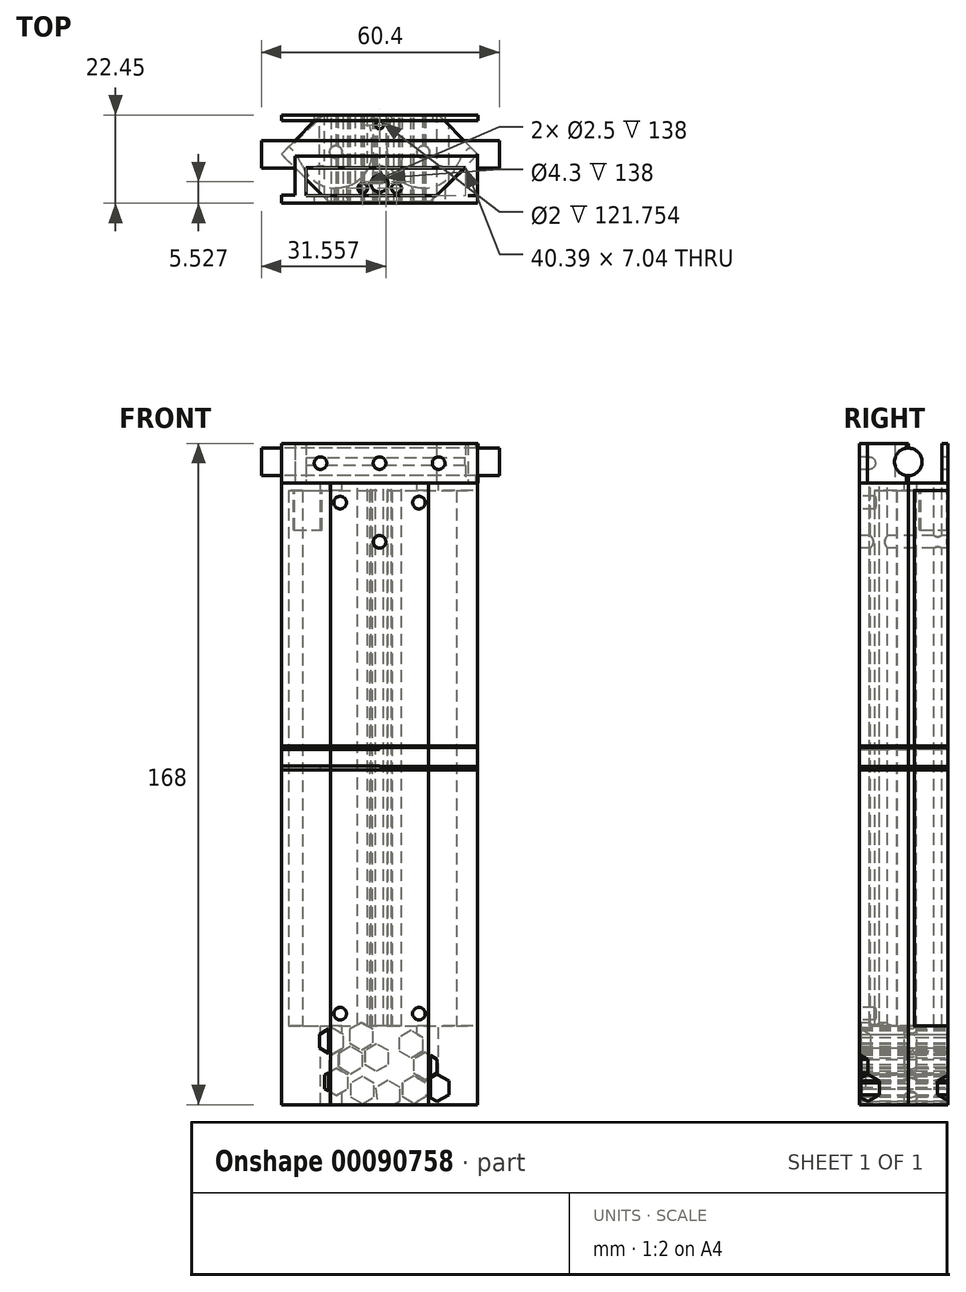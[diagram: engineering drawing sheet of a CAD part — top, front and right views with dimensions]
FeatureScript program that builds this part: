
annotation { "Feature Type Name" : "Feature", "Feature Type Description" : "" }
export const myFeature = defineFeature(function(context is Context, id is Id, definition is map)
    precondition{}
    {
        {
            var Q0;
            Q0=qCreatedBy(makeId("Top.planeOp"),FACE);
            var sketch = newSketch(context, id + "F0", { "sketchPlane" : qUnion([Q0])});
            skCircle(sketch, "E0.0", {"center": v(28.34, -87.3) * mm, "radius": 1 * mm});
            skCircle(sketch, "E0.1", {"center": v(39.24, -83.4) * mm, "radius": 2 * mm});
            skCircle(sketch, "E0.2", {"center": v(60.56, -76.3) * mm, "radius": 2.01 * mm});
            skCircle(sketch, "E0.3", {"center": v(29.67, -76.3) * mm, "radius": 9.48 * mm});
            skCircle(sketch, "E0.4", {"center": v(48.77, -76.3) * mm, "radius": 9.48 * mm});
            skLineSegment(sketch, "E0.5", {"start": v(64.18, -76.3) * mm, "end": v(14.3, -76.3) * mm});
            skLineSegment(sketch, "E0.6", {"start": v(14.3, -76.3) * mm, "end": v(24.27, -66.32) * mm});
            skLineSegment(sketch, "E0.7", {"start": v(24.27, -66.32) * mm, "end": v(52.19, -66.32) * mm});
            skLineSegment(sketch, "E0.8", {"start": v(52.19, -66.32) * mm, "end": v(64.18, -76.3) * mm});
            skCircle(sketch, "E0.9", {"center": v(50.63, -87.21) * mm, "radius": 1 * mm});
            skCircle(sketch, "E0.10", {"center": v(32.98, -87.04) * mm, "radius": 1 * mm});
            skCircle(sketch, "E0.11", {"center": v(45.91, -87.12) * mm, "radius": 1 * mm});
            skCircle(sketch, "E0.12", {"center": v(39.24, -69) * mm, "radius": 2 * mm});
            skLineSegment(sketch, "E0.13", {"start": v(26.76, -88.77) * mm, "end": v(51.7, -88.77) * mm});
            skCircle(sketch, "E0.14", {"center": v(17.86, -76.3) * mm, "radius": 2.02 * mm});
            skCircle(sketch, "E0.15", {"center": v(39.24, -69) * mm, "radius": 2 * mm});
            skCircle(sketch, "E0.16", {"center": v(39.24, -83.4) * mm, "radius": 2 * mm});
            skCircle(sketch, "E0.17", {"center": v(60.56, -76.3) * mm, "radius": 2.01 * mm});
            skCircle(sketch, "E0.18", {"center": v(17.86, -76.3) * mm, "radius": 2.02 * mm});
            skCircle(sketch, "E0.19", {"center": v(50.63, -87.21) * mm, "radius": 1 * mm});
            skCircle(sketch, "E0.20", {"center": v(28.34, -87.3) * mm, "radius": 1 * mm});
            skCircle(sketch, "E0.21", {"center": v(32.98, -87.04) * mm, "radius": 1 * mm});
            skCircle(sketch, "E0.22", {"center": v(45.91, -87.12) * mm, "radius": 1 * mm});
            skCircle(sketch, "E0.23", {"center": v(39.24, -69) * mm, "radius": 2 * mm});
            skCircle(sketch, "E0.24", {"center": v(39.24, -83.4) * mm, "radius": 2 * mm});
            skCircle(sketch, "E0.25", {"center": v(60.56, -76.3) * mm, "radius": 2.01 * mm});
            skCircle(sketch, "E0.26", {"center": v(17.86, -76.3) * mm, "radius": 2.02 * mm});
            skCircle(sketch, "E0.27", {"center": v(50.63, -87.21) * mm, "radius": 1 * mm});
            skCircle(sketch, "E0.28", {"center": v(28.34, -87.3) * mm, "radius": 1 * mm});
            skCircle(sketch, "E0.29", {"center": v(32.98, -87.04) * mm, "radius": 1 * mm});
            skCircle(sketch, "E0.30", {"center": v(45.91, -87.12) * mm, "radius": 1 * mm});
            skLineSegment(sketch, "E1", {"start": v(64.18, -76.3) * mm, "end": v(51.7, -88.77) * mm});
            skLineSegment(sketch, "E2", {"start": v(26.76, -88.77) * mm, "end": v(14.3, -76.3) * mm});
            skLineSegment(sketch, "E3", {"start": v(51.7, -88.77) * mm, "end": v(39.26, -101.25) * mm});
            skLineSegment(sketch, "E4", {"start": v(39.26, -101.25) * mm, "end": v(26.76, -88.77) * mm});
            skCircle(sketch, "E5.3", {"center": v(-36.32, -74.95) * mm, "radius": 9.2 * mm});
            skLineSegment(sketch, "E5.6", {"start": v(-50.16, -75.51) * mm, "end": v(-40.22, -65.55) * mm});
            skLineSegment(sketch, "E5.7", {"start": v(-40.22, -65.55) * mm, "end": v(-25.22, -65.56) * mm});
            skLineSegment(sketch, "E6", {"start": v(-12.73, -88) * mm, "end": v(-25.24, -100.46) * mm});
            skLineSegment(sketch, "E7", {"start": v(-25.24, -100.46) * mm, "end": v(-25.22, -65.56) * mm, "construction": true});
            skLineSegment(sketch, "E8", {"start": v(-50.16, -75.51) * mm, "end": v(-37.7, -87.98) * mm});
            skCircle(sketch, "E9.MirrorC", {"center": v(-14.12, -74.97) * mm, "radius": 9.2 * mm});
            skLineSegment(sketch, "E10.MirrorCS", {"start": v(-0.28, -75.54) * mm, "end": v(-25.24, -100.46) * mm});
            skLineSegment(sketch, "E11.MirrorCS", {"start": v(-0.28, -75.54) * mm, "end": v(-10.22, -65.57) * mm});
            skLineSegment(sketch, "E12.MirrorCS", {"start": v(-10.22, -65.57) * mm, "end": v(-25.22, -65.56) * mm});
            skLineSegment(sketch, "E13.MirrorCS", {"start": v(-37.73, -87.98) * mm, "end": v(-25.24, -100.46) * mm});
            skPoint(sketch, "E14.trimOffspring.start.orphan", {"position": v(-25.27, -75.46) * mm});
            skPoint(sketch, "E15.orphan", {"position": v(-50.27, -75.46) * mm});
            skLineSegment(sketch, "E16", {"start": v(-37.73, -87.98) * mm, "end": v(-12.73, -88) * mm});
            skFitSpline(sketch, "E17", {"points": [v(-27.12, -74.95) * mm, v(-29.63, -65.56) * mm, v(-72.25, -74.23) * mm], "startDerivative": vector(-1.55, 35.66) * mm, "endDerivative": vector(-79.61, -26.9) * mm});
            skFitSpline(sketch, "E18.MirrorCS", {"points": [v(-23.32, -74.96) * mm, v(-20.8, -65.56) * mm, v(21.8, -74.28) * mm], "startDerivative": vector(1.59, 35.66) * mm, "endDerivative": vector(79.58, -26.99) * mm});
            skFitSpline(sketch, "E19", {"points": [v(-44.25, -79.62) * mm, v(-48.33, -73.68) * mm, v(-51.27, -73.94) * mm], "startDerivative": vector(-6.44, 12.9) * mm, "endDerivative": vector(-7.7, -2.7) * mm});
            skFitSpline(sketch, "E20.MirrorCS", {"points": [v(-6.2, -79.64) * mm, v(-2.1, -73.7) * mm, v(0.83, -73.97) * mm], "startDerivative": vector(6.46, 12.9) * mm, "endDerivative": vector(7.7, -2.71) * mm});
            skSolve(sketch);
        }
        {
            var Q0;
            {var subQ18=sQuery(id+"F0.wireOp",EDGE,"E8");Q0=makeQuery(id+"F0.imprint","IMPRINT",FACE,{"disambiguationData":[TD([[makeQuery(id+"F0.imprint","IMPRINT",EDGE,{"derivedFrom":subQ18}),1.0]])]});}
            extrude(context, id + "F1", {"entities" : qUnion([Q0]), "depth" : 138 * mm});
        }
        {
            var Q0;
            Q0=makeQuery(id+"F1.opExtrude","CAP_FACE",FACE,{"disambiguationData":[OSD([sQuery(id+"F0.wireOp",EDGE,"E5.3"),sQuery(id+"F0.wireOp",EDGE,"E5.6"),sQuery(id+"F0.wireOp",EDGE,"E5.7"),sQuery(id+"F0.wireOp",EDGE,"E8"),sQuery(id+"F0.wireOp",EDGE,"E9.MirrorC"),sQuery(id+"F0.wireOp",EDGE,"E10.MirrorCS"),sQuery(id+"F0.wireOp",EDGE,"E11.MirrorCS"),sQuery(id+"F0.wireOp",EDGE,"E12.MirrorCS"),sQuery(id+"F0.wireOp",EDGE,"E16"),sQuery(id+"F0.wireOp",EDGE,"E17"),sQuery(id+"F0.wireOp",EDGE,"28ce3c09-6c9a-4552-adf3-a01f3755cea0"),sQuery(id+"F0.wireOp",EDGE,"77121457-b61a-4b0d-bc9d-ba2fe8860e380.MirrorCS"),sQuery(id+"F0.wireOp",EDGE,"E18.MirrorCS")])],"isStart":false});
            var sketch = newSketch(context, id + "F2", { "sketchPlane" : qUnion([Q0])});
            skLineSegment(sketch, "E21.0", {"start": v(-40.22, -65.55) * mm, "end": v(-25.22, -65.56) * mm});
            skLineSegment(sketch, "E21.1", {"start": v(-10.22, -65.57) * mm, "end": v(-25.22, -65.56) * mm});
            skLineSegment(sketch, "E21.2", {"start": v(-0.28, -75.54) * mm, "end": v(-10.22, -65.57) * mm});
            skLineSegment(sketch, "E21.3", {"start": v(-0.28, -75.54) * mm, "end": v(-12.75, -88) * mm});
            skLineSegment(sketch, "E21.4", {"start": v(-50.16, -75.51) * mm, "end": v(-37.7, -87.98) * mm});
            skLineSegment(sketch, "E21.5", {"start": v(-50.16, -75.51) * mm, "end": v(-40.22, -65.55) * mm});
            skLineSegment(sketch, "E22.0", {"start": v(-37.7, -87.98) * mm, "end": v(-12.75, -88) * mm});
            skPoint(sketch, "E23.orphan", {"position": v(-37.7, -87.98) * mm});
            skPoint(sketch, "E24.orphan", {"position": v(-25.24, -100.46) * mm});
            skSolve(sketch);
        }
        {
            var Q0;
            Q0 = qSketchRegion(id + "F2", true);
            var Q1;
            Q1=sQuery(id+"F0.wireOp",EDGE,"E12.MirrorCS");
            var Q2;
            Q2=sQuery(id+"F0.wireOp",EDGE,"E5.7");
            var Q3;
            Q3=sQuery(id+"F0.wireOp",EDGE,"E5.6");
            var Q4;
            Q4=sQuery(id+"F0.wireOp",EDGE,"E8");
            var Q5;
            Q5=sQuery(id+"F0.wireOp",EDGE,"E6");
            var Q6;
            Q6=sQuery(id+"F0.wireOp",EDGE,"E10.MirrorCS");
            var Q7;
            Q7=sQuery(id+"F0.wireOp",EDGE,"E11.MirrorCS");
            extrude(context, id + "F3", {"entities" : qUnion([Q0]), "operationType" : NewBodyOperationType.ADD, "surfaceEntities" : qUnion([Q1, Q2, Q3, Q4, Q5, Q6, Q7]), "oppositeDirection" : true, "depth" : 2 * mm});
        }
        {
            var Q0;
            Q0=makeQuery(id+"F1.opExtrude","SWEPT_FACE",FACE,{"disambiguationData":[OSD([sQuery(id+"F0.wireOp",EDGE,"E16")])]});
            var sketch = newSketch(context, id + "F4", { "sketchPlane" : qUnion([Q0])});
            skLineSegment(sketch, "E25", {"start": v(-25.18, 140) * mm, "end": v(-25.18, 71.2) * mm, "construction": true});
            skLineSegment(sketch, "E26.0", {"start": v(-50.12, 138) * mm, "end": v(-50.12, 0) * mm, "construction": true});
            skLineSegment(sketch, "E27", {"start": v(-50.12, 65.9) * mm, "end": v(-50.12, 65.1) * mm});
            skLineSegment(sketch, "E28", {"start": v(-50.12, 65.1) * mm, "end": v(-0.24, 65.1) * mm});
            skLineSegment(sketch, "E29", {"start": v(-0.24, 65.1) * mm, "end": v(-0.24, 65.9) * mm});
            skLineSegment(sketch, "E30", {"start": v(-50.12, 70.8) * mm, "end": v(-50.12, 71.2) * mm});
            skLineSegment(sketch, "E31", {"start": v(-50.12, 71.2) * mm, "end": v(-0.24, 71.2) * mm});
            skLineSegment(sketch, "E32.MirrorCS", {"start": v(-50.12, 70.4) * mm, "end": v(-0.24, 70.8) * mm});
            skLineSegment(sketch, "E33", {"start": v(-0.24, 71.2) * mm, "end": v(-0.24, 70.8) * mm});
            skLineSegment(sketch, "E34", {"start": v(-50.12, 70.8) * mm, "end": v(-50.12, 70.4) * mm});
            skLineSegment(sketch, "E35.0", {"start": v(-20.76, 136) * mm, "end": v(-10.18, 136) * mm, "construction": true});
            skLineSegment(sketch, "E36", {"start": v(-0.24, 65.9) * mm, "end": v(-50.12, 65.9) * mm});
            skPoint(sketch, "E37.orphan", {"position": v(-50.12, 69) * mm});
            skLineSegment(sketch, "E38", {"start": v(-25.18, 65.1) * mm, "end": v(-25.18, 65.9) * mm});
            skLineSegment(sketch, "E39.trimOffspring", {"start": v(-25.18, 65.1) * mm, "end": v(-25.18, 0) * mm, "construction": true});
            skLineSegment(sketch, "E40.trimOffspring", {"start": v(-25.18, 70.6) * mm, "end": v(-25.18, 65.9) * mm, "construction": true});
            skLineSegment(sketch, "E41", {"start": v(-25.18, 70.6) * mm, "end": v(-25.18, 71.2) * mm});
            skLineSegment(sketch, "E42", {"start": v(-50.12, 65.9) * mm, "end": v(-50.12, 66.1) * mm});
            skLineSegment(sketch, "E43", {"start": v(-50.12, 66.1) * mm, "end": v(-25.18, 66.1) * mm});
            skLineSegment(sketch, "E44", {"start": v(-25.18, 66.1) * mm, "end": v(-25.18, 65.9) * mm});
            skLineSegment(sketch, "E45", {"start": v(-50.12, 65.5) * mm, "end": v(-25.18, 65.5) * mm, "construction": true});
            skLineSegment(sketch, "E46", {"start": v(-50.12, 70.4) * mm, "end": v(-50.12, 70.2) * mm});
            skLineSegment(sketch, "E47", {"start": v(-50.12, 70.2) * mm, "end": v(-25.18, 70.2) * mm});
            skLineSegment(sketch, "E48", {"start": v(-25.18, 70.2) * mm, "end": v(-25.18, 70.6) * mm});
            skSolve(sketch);
        }
        {
            var Q0;
            Q0 = qSketchRegion(id + "F4", true);
            var Q1;
            Q1=makeQuery(id+"F3.boolean.opBoolean","MERGE",FACE,{"derivedFrom":[makeQuery(id+"F1.opExtrude","SWEPT_FACE",FACE,{"disambiguationData":[OSD([sQuery(id+"F0.wireOp",EDGE,"E5.7"),sQuery(id+"F0.wireOp",EDGE,"E12.MirrorCS")])]}),makeQuery(id+"F3.opExtrude","SWEPT_FACE",FACE,{"disambiguationData":[OSD([sQuery(id+"F2.wireOp",EDGE,"E21.0"),sQuery(id+"F2.wireOp",EDGE,"E21.1")])]})]});
            extrude(context, id + "F5", {"entities" : qUnion([Q0]), "endBound" : BoundingType.UP_TO_SURFACE, "oppositeDirection" : true, "endBoundEntityFace" : qUnion([Q1]), "depth" : 25 * mm});
        }
        {
            var Q0;
            {var subQ18=sQuery(id+"F0.wireOp",EDGE,"E8");Q0=makeQuery(id+"F0.imprint","IMPRINT",FACE,{"disambiguationData":[TD([[makeQuery(id+"F0.imprint","IMPRINT",EDGE,{"derivedFrom":subQ18}),1.0]])]});}
            var sketch = newSketch(context, id + "F6", { "sketchPlane" : qUnion([Q0])});
            skLineSegment(sketch, "E49.0", {"start": v(-50.16, -75.51) * mm, "end": v(-40.22, -65.55) * mm});
            skLineSegment(sketch, "E49.1", {"start": v(-40.22, -65.55) * mm, "end": v(-25.22, -65.56) * mm});
            skLineSegment(sketch, "E49.2", {"start": v(-10.22, -65.57) * mm, "end": v(-25.22, -65.56) * mm});
            skLineSegment(sketch, "E49.3", {"start": v(-0.28, -75.54) * mm, "end": v(-10.22, -65.57) * mm});
            skLineSegment(sketch, "E49.4", {"start": v(-0.28, -75.54) * mm, "end": v(-12.75, -88) * mm});
            skLineSegment(sketch, "E49.5", {"start": v(-37.73, -87.98) * mm, "end": v(-12.73, -88) * mm});
            skLineSegment(sketch, "E49.6", {"start": v(-50.16, -75.51) * mm, "end": v(-37.7, -87.98) * mm});
            skPoint(sketch, "E50.orphan", {"position": v(-25.24, -100.46) * mm});
            skPoint(sketch, "E51.orphan", {"position": v(-37.7, -87.98) * mm});
            skLineSegment(sketch, "E52.2", {"start": v(-0.3, -88) * mm, "end": v(-50.17, -87.97) * mm});
            skSolve(sketch);
        }
        {
            var Q0;
            Q0 = qSketchRegion(id + "F6", true);
            var Q1;
            Q1 = qSketchRegion(id + "F8", true);
            extrude(context, id + "F7", {"entities" : qUnion([Q0, Q1]), "operationType" : NewBodyOperationType.ADD, "oppositeDirection" : true, "depth" : 20 * mm});
        }
        {
            var Q0;
            Q0=makeQuery(id+"F7.boolean.opBoolean","MERGE",FACE,{"derivedFrom":[makeQuery(id+"F3.boolean.opBoolean","MERGE",FACE,{"derivedFrom":[makeQuery(id+"F1.opExtrude","SWEPT_FACE",FACE,{"disambiguationData":[OSD([sQuery(id+"F0.wireOp",EDGE,"E5.7"),sQuery(id+"F0.wireOp",EDGE,"E12.MirrorCS")])]}),makeQuery(id+"F3.opExtrude","SWEPT_FACE",FACE,{"disambiguationData":[OSD([sQuery(id+"F2.wireOp",EDGE,"E21.0"),sQuery(id+"F2.wireOp",EDGE,"E21.1")])]})]}),makeQuery(id+"F7.opExtrude","SWEPT_FACE",FACE,{"disambiguationData":[OSD([sQuery(id+"F6.wireOp",EDGE,"E49.1"),sQuery(id+"F6.wireOp",EDGE,"E49.2")])]})]});
            var sketch = newSketch(context, id + "F8", { "sketchPlane" : qUnion([Q0])});
            skCircle(sketch, "E53.cCircle", {"center": v(36.14, -14.2) * mm, "radius": 3 * mm, "construction": true});
            skLineSegment(sketch, "E53.0", {"start": v(33.14, -12.47) * mm, "end": v(36.14, -10.74) * mm});
            skLineSegment(sketch, "E53.1", {"start": v(36.14, -10.74) * mm, "end": v(39.14, -12.47) * mm});
            skLineSegment(sketch, "E53.2", {"start": v(39.14, -12.47) * mm, "end": v(39.14, -15.94) * mm});
            skLineSegment(sketch, "E53.3", {"start": v(39.14, -15.94) * mm, "end": v(36.14, -17.67) * mm});
            skLineSegment(sketch, "E53.4", {"start": v(36.14, -17.67) * mm, "end": v(33.14, -15.94) * mm});
            skLineSegment(sketch, "E53.5", {"start": v(33.14, -15.94) * mm, "end": v(33.14, -12.47) * mm});
            skPoint(sketch, "E53.0.midPoint", {"position": v(34.64, -11.6) * mm});
            skLineSegment(sketch, "E54", {"start": v(36.14, -17.67) * mm, "end": v(36.14, 0) * mm, "construction": true});
            skCircle(sketch, "E55.cCircle", {"center": v(37.4, -3.84) * mm, "radius": 3 * mm, "construction": true});
            skLineSegment(sketch, "E55.0", {"start": v(34.4, -2.1) * mm, "end": v(37.4, -0.38) * mm});
            skLineSegment(sketch, "E55.1", {"start": v(37.4, -0.38) * mm, "end": v(40.4, -2.1) * mm});
            skLineSegment(sketch, "E55.2", {"start": v(40.4, -2.1) * mm, "end": v(40.4, -5.57) * mm});
            skLineSegment(sketch, "E55.3", {"start": v(40.4, -5.57) * mm, "end": v(37.4, -7.3) * mm});
            skLineSegment(sketch, "E55.4", {"start": v(37.4, -7.3) * mm, "end": v(34.4, -5.57) * mm});
            skLineSegment(sketch, "E55.5", {"start": v(34.4, -5.57) * mm, "end": v(34.4, -2.1) * mm});
            skPoint(sketch, "E55.0.midPoint", {"position": v(35.9, -1.24) * mm});
            skCircle(sketch, "E56.cCircle", {"center": v(32.54, -8.66) * mm, "radius": 3 * mm, "construction": true});
            skLineSegment(sketch, "E56.0", {"start": v(29.54, -6.93) * mm, "end": v(32.54, -5.2) * mm});
            skLineSegment(sketch, "E56.1", {"start": v(32.54, -5.2) * mm, "end": v(35.54, -6.93) * mm});
            skLineSegment(sketch, "E56.2", {"start": v(35.54, -6.93) * mm, "end": v(35.54, -10.4) * mm});
            skLineSegment(sketch, "E56.3", {"start": v(35.54, -10.4) * mm, "end": v(32.54, -12.13) * mm});
            skLineSegment(sketch, "E56.4", {"start": v(32.54, -12.13) * mm, "end": v(29.54, -10.4) * mm});
            skLineSegment(sketch, "E56.5", {"start": v(29.54, -10.4) * mm, "end": v(29.54, -6.93) * mm});
            skPoint(sketch, "E56.0.midPoint", {"position": v(31.04, -6.07) * mm});
            skCircle(sketch, "E57.cCircle", {"center": v(29.54, -16.34) * mm, "radius": 3 * mm, "construction": true});
            skLineSegment(sketch, "E57.0", {"start": v(26.54, -14.6) * mm, "end": v(29.54, -12.87) * mm});
            skLineSegment(sketch, "E57.1", {"start": v(29.54, -12.87) * mm, "end": v(32.54, -14.6) * mm});
            skLineSegment(sketch, "E57.2", {"start": v(32.54, -14.6) * mm, "end": v(32.54, -18.07) * mm});
            skLineSegment(sketch, "E57.3", {"start": v(32.54, -18.07) * mm, "end": v(29.54, -19.8) * mm});
            skLineSegment(sketch, "E57.4", {"start": v(29.54, -19.8) * mm, "end": v(26.54, -18.07) * mm});
            skLineSegment(sketch, "E57.5", {"start": v(26.54, -18.07) * mm, "end": v(26.54, -14.6) * mm});
            skPoint(sketch, "E57.0.midPoint", {"position": v(28.04, -13.74) * mm});
            skCircle(sketch, "E58.cCircle", {"center": v(23.01, -17.31) * mm, "radius": 3 * mm, "construction": true});
            skLineSegment(sketch, "E58.0", {"start": v(20.01, -15.58) * mm, "end": v(23.01, -13.85) * mm});
            skLineSegment(sketch, "E58.1", {"start": v(23.01, -13.85) * mm, "end": v(26.26, -15.72) * mm});
            skLineSegment(sketch, "E58.2", {"start": v(26.26, -15.72) * mm, "end": v(25.7, -19.8) * mm});
            skLineSegment(sketch, "E58.4", {"start": v(21.51, -19.9) * mm, "end": v(20.01, -19.04) * mm});
            skLineSegment(sketch, "E58.5", {"start": v(20.01, -19.04) * mm, "end": v(20.01, -15.58) * mm});
            skPoint(sketch, "E58.0.midPoint", {"position": v(21.51, -14.71) * mm});
            skCircle(sketch, "E59.cCircle", {"center": v(29.82, -2.61) * mm, "radius": 3 * mm, "construction": true});
            skLineSegment(sketch, "E59.0", {"start": v(26.82, -0.88) * mm, "end": v(29.82, 0.85) * mm});
            skLineSegment(sketch, "E59.1", {"start": v(29.82, 0.85) * mm, "end": v(32.82, -0.88) * mm});
            skLineSegment(sketch, "E59.2", {"start": v(32.82, -0.88) * mm, "end": v(32.82, -4.35) * mm});
            skLineSegment(sketch, "E59.3", {"start": v(32.82, -4.35) * mm, "end": v(29.82, -6.08) * mm});
            skLineSegment(sketch, "E59.4", {"start": v(29.82, -6.08) * mm, "end": v(26.82, -4.35) * mm});
            skLineSegment(sketch, "E59.5", {"start": v(26.82, -4.35) * mm, "end": v(26.82, -0.88) * mm});
            skPoint(sketch, "E59.0.midPoint", {"position": v(28.32, -0.02) * mm});
            skCircle(sketch, "E60.cCircle", {"center": v(25.94, -8) * mm, "radius": 3 * mm, "construction": true});
            skLineSegment(sketch, "E60.0", {"start": v(22.94, -6.27) * mm, "end": v(25.94, -4.53) * mm});
            skLineSegment(sketch, "E60.1", {"start": v(25.94, -4.53) * mm, "end": v(28.94, -6.27) * mm});
            skLineSegment(sketch, "E60.2", {"start": v(28.94, -6.27) * mm, "end": v(28.94, -9.73) * mm});
            skLineSegment(sketch, "E60.3", {"start": v(28.94, -9.73) * mm, "end": v(25.94, -11.46) * mm});
            skLineSegment(sketch, "E60.4", {"start": v(25.94, -11.46) * mm, "end": v(22.94, -9.73) * mm});
            skLineSegment(sketch, "E60.5", {"start": v(22.94, -9.73) * mm, "end": v(22.94, -6.27) * mm});
            skPoint(sketch, "E60.0.midPoint", {"position": v(24.44, -5.4) * mm});
            skCircle(sketch, "E61.cCircle", {"center": v(16.41, -16.2) * mm, "radius": 3 * mm, "construction": true});
            skLineSegment(sketch, "E61.0", {"start": v(13.41, -14.46) * mm, "end": v(16.41, -12.73) * mm});
            skLineSegment(sketch, "E61.1", {"start": v(16.41, -12.73) * mm, "end": v(19.41, -14.46) * mm});
            skLineSegment(sketch, "E61.2", {"start": v(19.41, -14.46) * mm, "end": v(19.41, -17.93) * mm});
            skLineSegment(sketch, "E61.3", {"start": v(19.41, -17.93) * mm, "end": v(16.41, -19.66) * mm});
            skLineSegment(sketch, "E61.4", {"start": v(16.41, -19.66) * mm, "end": v(13.41, -17.93) * mm});
            skLineSegment(sketch, "E61.5", {"start": v(13.41, -17.93) * mm, "end": v(13.41, -14.46) * mm});
            skPoint(sketch, "E61.0.midPoint", {"position": v(14.91, -13.6) * mm});
            skLineSegment(sketch, "E62", {"start": v(25.7, -19.8) * mm, "end": v(21.51, -19.9) * mm});
            skLineSegment(sketch, "E63.5", {"start": v(14.2, -17.46) * mm, "end": v(14.2, -14) * mm});
            skPoint(sketch, "E63.0.midPoint", {"position": v(15.7, -13.13) * mm});
            skCircle(sketch, "E64.cCircle", {"center": v(17.2, -4.65) * mm, "radius": 3 * mm, "construction": true});
            skLineSegment(sketch, "E64.0", {"start": v(14.2, -2.91) * mm, "end": v(17.2, -1.18) * mm});
            skLineSegment(sketch, "E64.1", {"start": v(17.2, -1.18) * mm, "end": v(20.2, -2.91) * mm});
            skLineSegment(sketch, "E64.2", {"start": v(20.2, -2.91) * mm, "end": v(20.2, -6.38) * mm});
            skLineSegment(sketch, "E64.3", {"start": v(20.2, -6.38) * mm, "end": v(17.2, -8.1) * mm});
            skLineSegment(sketch, "E64.4", {"start": v(17.2, -8.1) * mm, "end": v(14.2, -6.38) * mm});
            skLineSegment(sketch, "E64.5", {"start": v(14.2, -6.38) * mm, "end": v(14.2, -2.91) * mm});
            skPoint(sketch, "E64.0.midPoint", {"position": v(15.7, -2.05) * mm});
            skCircle(sketch, "E65.cCircle", {"center": v(13.6, -10.19) * mm, "radius": 3 * mm, "construction": true});
            skLineSegment(sketch, "E65.0", {"start": v(10.6, -8.46) * mm, "end": v(13.6, -6.72) * mm});
            skLineSegment(sketch, "E65.1", {"start": v(13.6, -6.72) * mm, "end": v(16.6, -8.46) * mm});
            skLineSegment(sketch, "E65.2", {"start": v(16.6, -8.46) * mm, "end": v(16.6, -11.92) * mm});
            skLineSegment(sketch, "E65.3", {"start": v(16.6, -11.92) * mm, "end": v(13.6, -13.65) * mm});
            skLineSegment(sketch, "E65.4", {"start": v(13.6, -13.65) * mm, "end": v(10.6, -11.92) * mm});
            skLineSegment(sketch, "E65.5", {"start": v(10.6, -11.92) * mm, "end": v(10.6, -8.46) * mm});
            skPoint(sketch, "E65.0.midPoint", {"position": v(12.1, -7.59) * mm});
            skCircle(sketch, "E66.cCircle", {"center": v(10.6, -15.73) * mm, "radius": 3 * mm, "construction": true});
            skLineSegment(sketch, "E66.0", {"start": v(7.6, -14) * mm, "end": v(10.6, -12.27) * mm});
            skLineSegment(sketch, "E66.1", {"start": v(10.6, -12.27) * mm, "end": v(13.6, -14) * mm});
            skLineSegment(sketch, "E66.2", {"start": v(13.6, -14) * mm, "end": v(13.6, -17.46) * mm});
            skLineSegment(sketch, "E66.3", {"start": v(13.6, -17.46) * mm, "end": v(10.6, -19.2) * mm});
            skLineSegment(sketch, "E66.4", {"start": v(10.6, -19.2) * mm, "end": v(7.6, -17.46) * mm});
            skLineSegment(sketch, "E66.5", {"start": v(7.6, -17.46) * mm, "end": v(7.6, -14) * mm});
            skPoint(sketch, "E66.0.midPoint", {"position": v(9.1, -13.13) * mm});
            skSolve(sketch);
        }
        {
            var Q0;
            Q0 = qSketchRegion(id + "F8", true);
            var Q1;
            Q1=sQuery(id+"F8.wireOp",EDGE,"a0639ec5-36db-4593-97fa-c94961bb7019.1");
            var Q2;
            Q2=sQuery(id+"F8.wireOp",EDGE,"55600522-a46f-4de3-be34-bca631a758cf.4");
            var Q3;
            Q3=sQuery(id+"F8.wireOp",EDGE,"ffd1e3c1-856c-4fb0-91cf-635109e7a11e.5");
            var Q4;
            Q4=makeQuery(id+"F7.boolean.opBoolean","MERGE",FACE,{"derivedFrom":[makeQuery(id+"F1.opExtrude","SWEPT_FACE",FACE,{"disambiguationData":[OSD([sQuery(id+"F0.wireOp",EDGE,"E16")])]}),makeQuery(id+"F7.opExtrude","SWEPT_FACE",FACE,{"disambiguationData":[OSD([sQuery(id+"F6.wireOp",EDGE,"E52.2")])]})]});
            var Q5;
            Q5=makeQuery(id+"F1.opExtrude","SWEPT_BODY",BODY,{"disambiguationData":[OSD([sQuery(id+"F0.wireOp",EDGE,"E5.3"),sQuery(id+"F0.wireOp",EDGE,"E5.6"),sQuery(id+"F0.wireOp",EDGE,"E5.7"),sQuery(id+"F0.wireOp",EDGE,"E8"),sQuery(id+"F0.wireOp",EDGE,"E9.MirrorC"),sQuery(id+"F0.wireOp",EDGE,"E10.MirrorCS"),sQuery(id+"F0.wireOp",EDGE,"E11.MirrorCS"),sQuery(id+"F0.wireOp",EDGE,"E12.MirrorCS"),sQuery(id+"F0.wireOp",EDGE,"E16"),sQuery(id+"F0.wireOp",EDGE,"E17"),sQuery(id+"F0.wireOp",EDGE,"E18.MirrorCS"),sQuery(id+"F0.wireOp",EDGE,"E19"),sQuery(id+"F0.wireOp",EDGE,"E20.MirrorCS")])]});
            extrude(context, id + "F9", {"entities" : qUnion([Q0]), "operationType" : NewBodyOperationType.REMOVE, "surfaceEntities" : qUnion([Q1, Q2, Q3]), "oppositeDirection" : true, "endBoundEntityFace" : qUnion([Q4]), "endBoundEntityBody" : qUnion([Q5]), "depth" : 22 * mm});
        }
        {
            var Q0;
            Q0=makeQuery(id+"F3.boolean.opBoolean","MERGE",FACE,{"derivedFrom":[makeQuery(id+"F1.opExtrude","CAP_FACE",FACE,{"disambiguationData":[OSD([sQuery(id+"F0.wireOp",EDGE,"E5.3"),sQuery(id+"F0.wireOp",EDGE,"E5.6"),sQuery(id+"F0.wireOp",EDGE,"E5.7"),sQuery(id+"F0.wireOp",EDGE,"E8"),sQuery(id+"F0.wireOp",EDGE,"E9.MirrorC"),sQuery(id+"F0.wireOp",EDGE,"E10.MirrorCS"),sQuery(id+"F0.wireOp",EDGE,"E11.MirrorCS"),sQuery(id+"F0.wireOp",EDGE,"E12.MirrorCS"),sQuery(id+"F0.wireOp",EDGE,"E16"),sQuery(id+"F0.wireOp",EDGE,"E17"),sQuery(id+"F0.wireOp",EDGE,"28ce3c09-6c9a-4552-adf3-a01f3755cea0"),sQuery(id+"F0.wireOp",EDGE,"77121457-b61a-4b0d-bc9d-ba2fe8860e380.MirrorCS"),sQuery(id+"F0.wireOp",EDGE,"E18.MirrorCS")])],"isStart":false}),makeQuery(id+"F3.opExtrude","CAP_FACE",FACE,{"disambiguationData":[OSD([sQuery(id+"F2.wireOp",EDGE,"E21.0"),sQuery(id+"F2.wireOp",EDGE,"E21.1"),sQuery(id+"F2.wireOp",EDGE,"E21.2"),sQuery(id+"F2.wireOp",EDGE,"E21.3"),sQuery(id+"F2.wireOp",EDGE,"E21.4"),sQuery(id+"F2.wireOp",EDGE,"E21.5"),sQuery(id+"F2.wireOp",EDGE,"E22.0")])],"isStart":true})]});
            var sketch = newSketch(context, id + "F10", { "sketchPlane" : qUnion([Q0])});
            skLineSegment(sketch, "E67.0", {"start": v(-0.28, -65.57) * mm, "end": v(-50.15, -65.55) * mm});
            skLineSegment(sketch, "E67.1", {"start": v(-50.15, -65.55) * mm, "end": v(-50.17, -87.97) * mm});
            skLineSegment(sketch, "E67.2", {"start": v(-50.17, -87.97) * mm, "end": v(-0.3, -88) * mm});
            skLineSegment(sketch, "E67.3", {"start": v(-0.28, -65.57) * mm, "end": v(-0.3, -88) * mm});
            skLineSegment(sketch, "E67.4", {"start": v(-0.28, -75.54) * mm, "end": v(-10.22, -65.57) * mm});
            skLineSegment(sketch, "E67.5", {"start": v(-50.16, -75.51) * mm, "end": v(-40.22, -65.55) * mm});
            skLineSegment(sketch, "E67.6", {"start": v(-50.16, -75.51) * mm, "end": v(-37.7, -87.98) * mm});
            skLineSegment(sketch, "E67.7", {"start": v(-0.28, -75.54) * mm, "end": v(-12.75, -88) * mm});
            skPoint(sketch, "E68.orphan", {"position": v(-37.7, -87.98) * mm});
            skPoint(sketch, "E69.orphan", {"position": v(-25.24, -100.46) * mm});
            skSolve(sketch);
        }
        {
            var Q0;
            {var subQ0=sQuery(id+"F10.wireOp",EDGE,"E67.4");Q0=makeQuery(id+"F10.imprint","IMPRINT",FACE,{"disambiguationData":[TD([[makeQuery(id+"F10.imprint","IMPRINT",EDGE,{"derivedFrom":subQ0}),-1.0]])]});}
            var Q1;
            {var subQ0=sQuery(id+"F10.wireOp",EDGE,"E67.7");Q1=makeQuery(id+"F10.imprint","IMPRINT",FACE,{"disambiguationData":[TD([[makeQuery(id+"F10.imprint","IMPRINT",EDGE,{"derivedFrom":subQ0}),1.0]])]});}
            var Q2;
            {var subQ0=sQuery(id+"F10.wireOp",EDGE,"E67.6");Q2=makeQuery(id+"F10.imprint","IMPRINT",FACE,{"disambiguationData":[TD([[makeQuery(id+"F10.imprint","IMPRINT",EDGE,{"derivedFrom":subQ0}),-1.0]])]});}
            var Q3;
            {var subQ0=sQuery(id+"F10.wireOp",EDGE,"E67.5");Q3=makeQuery(id+"F10.imprint","IMPRINT",FACE,{"disambiguationData":[TD([[makeQuery(id+"F10.imprint","IMPRINT",EDGE,{"derivedFrom":subQ0}),1.0]])]});}
            extrude(context, id + "F11", {"entities" : qUnion([Q0, Q1, Q2, Q3]), "operationType" : NewBodyOperationType.REMOVE, "oppositeDirection" : true, "depth" : 80 * mm});
        }
        {
            var Q0;
            Q0=makeQuery(id+"F3.boolean.opBoolean","MERGE",FACE,{"derivedFrom":[makeQuery(id+"F1.opExtrude","CAP_FACE",FACE,{"disambiguationData":[OSD([sQuery(id+"F0.wireOp",EDGE,"E5.3"),sQuery(id+"F0.wireOp",EDGE,"E5.6"),sQuery(id+"F0.wireOp",EDGE,"E5.7"),sQuery(id+"F0.wireOp",EDGE,"E8"),sQuery(id+"F0.wireOp",EDGE,"E9.MirrorC"),sQuery(id+"F0.wireOp",EDGE,"E10.MirrorCS"),sQuery(id+"F0.wireOp",EDGE,"E11.MirrorCS"),sQuery(id+"F0.wireOp",EDGE,"E12.MirrorCS"),sQuery(id+"F0.wireOp",EDGE,"E16"),sQuery(id+"F0.wireOp",EDGE,"E17"),sQuery(id+"F0.wireOp",EDGE,"28ce3c09-6c9a-4552-adf3-a01f3755cea0"),sQuery(id+"F0.wireOp",EDGE,"77121457-b61a-4b0d-bc9d-ba2fe8860e380.MirrorCS"),sQuery(id+"F0.wireOp",EDGE,"E18.MirrorCS")])],"isStart":false}),makeQuery(id+"F3.opExtrude","CAP_FACE",FACE,{"disambiguationData":[OSD([sQuery(id+"F2.wireOp",EDGE,"E21.0"),sQuery(id+"F2.wireOp",EDGE,"E21.1"),sQuery(id+"F2.wireOp",EDGE,"E21.2"),sQuery(id+"F2.wireOp",EDGE,"E21.3"),sQuery(id+"F2.wireOp",EDGE,"E21.4"),sQuery(id+"F2.wireOp",EDGE,"E21.5"),sQuery(id+"F2.wireOp",EDGE,"E22.0")])],"isStart":true})]});
            var sketch = newSketch(context, id + "F12", { "sketchPlane" : qUnion([Q0])});
            skLineSegment(sketch, "E70", {"start": v(-47.07, -72.42) * mm, "end": v(-46.79, -72.7) * mm});
            skLineSegment(sketch, "E71", {"start": v(-46.79, -72.7) * mm, "end": v(-39.9, -65.8) * mm});
            skLineSegment(sketch, "E72", {"start": v(-39.9, -65.8) * mm, "end": v(-40.22, -65.55) * mm});
            skLineSegment(sketch, "E73", {"start": v(-40.22, -65.55) * mm, "end": v(-47.07, -72.42) * mm});
            skSolve(sketch);
        }
        {
            var Q0;
            Q0 = qSketchRegion(id + "F12", true);
            extrude(context, id + "F13", {"entities" : qUnion([Q0]), "operationType" : NewBodyOperationType.ADD, "oppositeDirection" : true, "depth" : 12 * mm});
        }
        {
            var Q0;
            Q0=sQuery(id+"F8.wireOp",VERTEX,"beaefd44-ba20-4250-a120-67fa8c3cad5e22.MirrorC.center");
            var Q1;
            Q1=sQuery(id+"F0.wireOp",VERTEX,"E5.3.center");
            var Q2;
            Q2=sQuery(id+"F0.wireOp",VERTEX,"E9.MirrorC.center");
            var Q3;
            Q3=sQuery(id+"F8.wireOp",VERTEX,"67a7fc68-4d06-4ea4-b756-b77a01b885cd");
            var Q4;
            Q4=sQuery(id+"F8.wireOp",VERTEX,"ba3f2c93-48ea-41c1-9624-446072f71531");
            var Q5;
            Q5=makeQuery(id+"F1.opExtrude","SWEPT_BODY",BODY,{"disambiguationData":[OSD([sQuery(id+"F0.wireOp",EDGE,"E5.3"),sQuery(id+"F0.wireOp",EDGE,"E5.6"),sQuery(id+"F0.wireOp",EDGE,"E5.7"),sQuery(id+"F0.wireOp",EDGE,"E8"),sQuery(id+"F0.wireOp",EDGE,"E9.MirrorC"),sQuery(id+"F0.wireOp",EDGE,"E10.MirrorCS"),sQuery(id+"F0.wireOp",EDGE,"E11.MirrorCS"),sQuery(id+"F0.wireOp",EDGE,"E12.MirrorCS"),sQuery(id+"F0.wireOp",EDGE,"E16"),sQuery(id+"F0.wireOp",EDGE,"E17"),sQuery(id+"F0.wireOp",EDGE,"28ce3c09-6c9a-4552-adf3-a01f3755cea0"),sQuery(id+"F0.wireOp",EDGE,"77121457-b61a-4b0d-bc9d-ba2fe8860e380.MirrorCS"),sQuery(id+"F0.wireOp",EDGE,"E18.MirrorCS")])]});
            hole(context, id + "F14", {"style" : HoleStyle.SIMPLE, "endStyle" : HoleEndStyle.BLIND, "holeDiameter" : 3.2 * mm, "holeDepth" : 25 * mm, "locations" : qUnion([Q0, Q1, Q2, Q3, Q4]), "scope" : qUnion([Q5])});
        }
        {
            var Q0;
            {var subQ1=sQuery(id+"F10.wireOp",EDGE,"E67.4");Q0=makeQuery(id+"F10.imprint","IMPRINT",FACE,{"disambiguationData":[TD([[makeQuery(id+"F10.imprint","IMPRINT",EDGE,{"derivedFrom":subQ1}),1.0]])]});}
            var sketch = newSketch(context, id + "F15", { "sketchPlane" : qUnion([Q0])});
            skLineSegment(sketch, "E74.0", {"start": v(-50.17, -87.97) * mm, "end": v(-0.3, -88) * mm});
            skLineSegment(sketch, "E75.0", {"start": v(-39.7, -85.98) * mm, "end": v(-37.7, -87.98) * mm});
            skLineSegment(sketch, "E76.0", {"start": v(-10.75, -86) * mm, "end": v(-12.75, -88) * mm});
            skPoint(sketch, "E77.0", {"position": v(-36.32, -74.95) * mm});
            skPoint(sketch, "E78.0", {"position": v(-14.12, -74.97) * mm});
            skPoint(sketch, "E79.startSnap0", {"position": v(-0.28, -76.79) * mm});
            skLineSegment(sketch, "E80", {"start": v(-0.29, -86) * mm, "end": v(-50.16, -85.97) * mm});
            skLineSegment(sketch, "E81.trimOffspring", {"start": v(-50.16, -85.97) * mm, "end": v(-50.17, -87.97) * mm});
            skLineSegment(sketch, "E82.trimOffspring", {"start": v(-0.29, -86) * mm, "end": v(-0.3, -88) * mm});
            skPoint(sketch, "E83.orphan", {"position": v(-0.28, -65.57) * mm});
            skPoint(sketch, "E84.0.start.orphan", {"position": v(-50.15, -65.55) * mm});
            skPoint(sketch, "E85.orphan", {"position": v(-50.16, -75.51) * mm});
            skPoint(sketch, "E86.orphan", {"position": v(-0.28, -75.54) * mm});
            skLineSegment(sketch, "E87", {"start": v(-10.75, -86) * mm, "end": v(-0.28, -75.9) * mm});
            skLineSegment(sketch, "E88", {"start": v(-0.28, -75.54) * mm, "end": v(-0.28, -75.9) * mm});
            skLineSegment(sketch, "E89", {"start": v(-0.28, -75.54) * mm, "end": v(-11.12, -86) * mm});
            skLineSegment(sketch, "E90", {"start": v(-46.66, -76.04) * mm, "end": v(-46.66, -78.08) * mm});
            skPoint(sketch, "E91", {"position": v(-36.32, -86.98) * mm});
            skPoint(sketch, "E91.positionSnap0", {"position": v(-38.7, -86.98) * mm});
            skPoint(sketch, "E92", {"position": v(-14.12, -87) * mm});
            skPoint(sketch, "E92.positionSnap0", {"position": v(-11.75, -87) * mm});
            skPoint(sketch, "E93", {"position": v(-25.23, -86.98) * mm});
            skPoint(sketch, "E93.positionSnap0", {"position": v(-25.23, -87.98) * mm});
            skLineSegment(sketch, "E94.top", {"start": v(-50.15, -67.05) * mm, "end": v(-0.28, -67.05) * mm});
            skLineSegment(sketch, "E94.left", {"start": v(-50.15, -65.55) * mm, "end": v(-50.15, -67.05) * mm});
            skLineSegment(sketch, "E94.right", {"start": v(-0.28, -65.55) * mm, "end": v(-0.28, -67.05) * mm});
            skLineSegment(sketch, "E95.bottom", {"start": v(-46.66, -76.04) * mm, "end": v(-0.29, -76.04) * mm});
            skLineSegment(sketch, "E95.top", {"start": v(-46.66, -78.95) * mm, "end": v(-0.29, -78.95) * mm});
            skLineSegment(sketch, "E95.left", {"start": v(-46.66, -76.04) * mm, "end": v(-46.66, -78.95) * mm});
            skLineSegment(sketch, "E95.right", {"start": v(-0.29, -76.04) * mm, "end": v(-0.29, -78.95) * mm});
            skLineSegment(sketch, "E96.bottom", {"start": v(-46.66, -78.95) * mm, "end": v(-43.84, -78.95) * mm});
            skLineSegment(sketch, "E96.top", {"start": v(-46.66, -85.97) * mm, "end": v(-43.84, -85.97) * mm});
            skLineSegment(sketch, "E96.left", {"start": v(-46.66, -78.95) * mm, "end": v(-46.66, -85.97) * mm});
            skLineSegment(sketch, "E96.right", {"start": v(-43.84, -78.95) * mm, "end": v(-43.84, -85.97) * mm});
            skLineSegment(sketch, "E97.bottom", {"start": v(-0.29, -78.95) * mm, "end": v(-2.7, -78.95) * mm});
            skLineSegment(sketch, "E97.top", {"start": v(-0.29, -86) * mm, "end": v(-2.7, -86) * mm});
            skLineSegment(sketch, "E97.left", {"start": v(-0.29, -78.95) * mm, "end": v(-0.29, -86) * mm});
            skLineSegment(sketch, "E97.right", {"start": v(-2.7, -78.95) * mm, "end": v(-2.7, -86) * mm});
            skLineSegment(sketch, "E98", {"start": v(-50.15, -65.55) * mm, "end": v(-0.28, -65.55) * mm});
            skSolve(sketch);
        }
        {
            var Q0;
            Q0 = qSketchRegion(id + "F15", true);
            extrude(context, id + "F16", {"entities" : qUnion([Q0]), "depth" : 10 * mm});
        }
        {
            var Q0;
            Q0=makeQuery(id+"F16.opExtrude","SWEPT_FACE",FACE,{"disambiguationData":[OSD([sQuery(id+"F15.wireOp",EDGE,"E74.0")])]});
            var sketch = newSketch(context, id + "F17", { "sketchPlane" : qUnion([Q0])});
            skPoint(sketch, "E99", {"position": v(-25.18, 143) * mm});
            skPoint(sketch, "E99.positionSnap0", {"position": v(-25.18, 138) * mm});
            skPoint(sketch, "E99.positionSnap1", {"position": v(-50.12, 143) * mm});
            skPoint(sketch, "E100.0", {"position": v(-40.18, 138) * mm});
            skPoint(sketch, "E100.1", {"position": v(-10.18, 138) * mm});
            skPoint(sketch, "E100.2", {"position": v(-12.7, 138) * mm});
            skPoint(sketch, "E100.3", {"position": v(-37.66, 138) * mm});
            skPoint(sketch, "E101", {"position": v(-40.18, 143) * mm});
            skPoint(sketch, "E102", {"position": v(-10.18, 143) * mm});
            skSolve(sketch);
        }
        {
            var Q0;
            Q0=sQuery(id+"F15.wireOp",VERTEX,"E77.0");
            var Q1;
            Q1=sQuery(id+"F15.wireOp",VERTEX,"E78.0");
            var Q2;
            Q2=sQuery(id+"F17.wireOp",VERTEX,"E101");
            var Q3;
            Q3=sQuery(id+"F17.wireOp",VERTEX,"E99");
            var Q4;
            Q4=sQuery(id+"F17.wireOp",VERTEX,"E102");
            var Q5;
            Q5=makeQuery(id+"F16.opExtrude","SWEPT_BODY",BODY,{"disambiguationData":[OSD([sQuery(id+"F15.wireOp",EDGE,"E74.0"),sQuery(id+"F15.wireOp",EDGE,"E80"),sQuery(id+"F15.wireOp",EDGE,"E81.trimOffspring"),sQuery(id+"F15.wireOp",EDGE,"E82.trimOffspring"),sQuery(id+"F15.wireOp",EDGE,"E87"),sQuery(id+"F15.wireOp",EDGE,"nKC8Ekyp-c2aD-to8B-boQF-ZkO6KhN6bdIw"),sQuery(id+"F15.wireOp",EDGE,"E88"),sQuery(id+"F15.wireOp",EDGE,"E89"),sQuery(id+"F15.wireOp",EDGE,"E90"),sQuery(id+"F15.wireOp",EDGE,"WwqMPIPg-V26o-Nrur-8pl3-CYisy1ftwQyE")])]});
            var Q6;
            Q6=makeQuery(id+"F16.opExtrude","SWEPT_BODY",BODY,{"disambiguationData":[OSD([sQuery(id+"F15.wireOp",EDGE,"E94.bottom"),sQuery(id+"F15.wireOp",EDGE,"E94.top"),sQuery(id+"F15.wireOp",EDGE,"E94.left"),sQuery(id+"F15.wireOp",EDGE,"E94.right")])]});
            var Q7;
            Q7=makeQuery(id+"F1.opExtrude","SWEPT_BODY",BODY,{"disambiguationData":[OSD([sQuery(id+"F0.wireOp",EDGE,"E5.3"),sQuery(id+"F0.wireOp",EDGE,"E5.6"),sQuery(id+"F0.wireOp",EDGE,"E5.7"),sQuery(id+"F0.wireOp",EDGE,"E8"),sQuery(id+"F0.wireOp",EDGE,"E9.MirrorC"),sQuery(id+"F0.wireOp",EDGE,"E10.MirrorCS"),sQuery(id+"F0.wireOp",EDGE,"E11.MirrorCS"),sQuery(id+"F0.wireOp",EDGE,"E12.MirrorCS"),sQuery(id+"F0.wireOp",EDGE,"E16"),sQuery(id+"F0.wireOp",EDGE,"E17"),sQuery(id+"F0.wireOp",EDGE,"E18.MirrorCS"),sQuery(id+"F0.wireOp",EDGE,"E19"),sQuery(id+"F0.wireOp",EDGE,"E20.MirrorCS")])]});
            hole(context, id + "F18", {"style" : HoleStyle.SIMPLE, "endStyle" : HoleEndStyle.THROUGH, "holeDiameter" : 3.2 * mm, "locations" : qUnion([Q0, Q1, Q2, Q3, Q4]), "scope" : qUnion([Q5, Q6, Q7]), "isTappedThrough" : true});
        }
        {
            var Q0;
            Q0=makeQuery(id+"F1.opExtrude","SWEPT_EDGE",EDGE,{"disambiguationData":[OSD([sQuery(id+"F0.wireOp",EDGE,"E12.MirrorCS"),sQuery(id+"F0.wireOp",EDGE,"E18.MirrorCS")])]});
            var Q1;
            Q1=makeQuery(id+"F1.opExtrude","SWEPT_EDGE",EDGE,{"disambiguationData":[OSD([sQuery(id+"F0.wireOp",EDGE,"E11.MirrorCS"),sQuery(id+"F0.wireOp",EDGE,"E20.MirrorCS")])]});
            fillet(context, id + "F19", {"entities" : qUnion([Q0, Q1]), "radius" : 1 * mm, "tangentPropagation" : true, "allowEdgeOverflow" : false});
        }
        {
            var Q0;
            Q0=makeQuery(id+"F1.opExtrude","SWEPT_EDGE",EDGE,{"disambiguationData":[OSD([sQuery(id+"F0.wireOp",EDGE,"E5.7"),sQuery(id+"F0.wireOp",EDGE,"E17")])]});
            fillet(context, id + "F20", {"entities" : qUnion([Q0]), "radius" : 2 * mm, "tangentPropagation" : true, "allowEdgeOverflow" : false});
        }
        {
            var Q0;
            {var subQ1=sQuery(id+"F10.wireOp",EDGE,"E67.4");Q0=makeQuery(id+"F10.imprint","IMPRINT",FACE,{"disambiguationData":[TD([[makeQuery(id+"F10.imprint","IMPRINT",EDGE,{"derivedFrom":subQ1}),1.0]])]});}
            var sketch = newSketch(context, id + "F21", { "sketchPlane" : qUnion([Q0])});
            skLineSegment(sketch, "E103.0", {"start": v(-25.24, -100.46) * mm, "end": v(-25.22, -65.56) * mm, "construction": true});
            skLineSegment(sketch, "E104.0", {"start": v(-0.29, -86) * mm, "end": v(-50.16, -85.97) * mm, "construction": true});
            skCircle(sketch, "E105", {"center": v(-25.23, -83.01) * mm, "radius": 2.15 * mm});
            skCircle(sketch, "E106", {"center": v(-25.22, -68.09) * mm, "radius": 1 * mm});
            skCircle(sketch, "E107", {"center": v(-29.52, -84.15) * mm, "radius": 1.25 * mm});
            skCircle(sketch, "E108.MirrorC", {"center": v(-20.93, -84.16) * mm, "radius": 1.25 * mm});
            skSolve(sketch);
        }
        {
            var Q0;
            Q0 = qSketchRegion(id + "F21", true);
            extrude(context, id + "F22", {"entities" : qUnion([Q0]), "operationType" : NewBodyOperationType.REMOVE, "oppositeDirection" : true, "depth" : 138 * mm});
        }
        {
            var Q0;
            {var subQ0=sQuery(id+"F0.wireOp",EDGE,"E16");var subQ2=makeQuery(id+"F1.opExtrude","CAP_EDGE",EDGE,{"disambiguationData":[OSD([subQ0])],"isStart":false});Q0=makeQuery(id+"F4.imprint","IMPRINT",FACE,{"disambiguationData":[TD([[makeQuery(id+"F4.imprint","IMPRINT",EDGE,{"derivedFrom":subQ2}),-1.0]])]});}
            var sketch = newSketch(context, id + "F23", { "sketchPlane" : qUnion([Q0])});
            skLineSegment(sketch, "E109.0", {"start": v(-25.18, 140) * mm, "end": v(-25.18, 71.2) * mm, "construction": true});
            skPoint(sketch, "E110.0", {"position": v(-25.18, 143) * mm});
            skCircle(sketch, "E111", {"center": v(-25.18, 133) * mm, "radius": 10 * mm, "construction": true});
            skLineSegment(sketch, "E112", {"start": v(-25.18, 133) * mm, "end": v(-11.29, 133) * mm, "construction": true});
            skCircle(sketch, "E113.0", {"center": v(-25.18, 143) * mm, "radius": 1.6 * mm});
            skCircle(sketch, "E114.MirrorC", {"center": v(-25.18, 123) * mm, "radius": 1.6 * mm});
            skCircle(sketch, "E115.MirrorC", {"center": v(-15.17, 132.98) * mm, "radius": 1.6 * mm});
            skCircle(sketch, "E116.MirrorC", {"center": v(-35.2, 132.98) * mm, "radius": 1.6 * mm});
            skLineSegment(sketch, "E117.1", {"start": v(-25.18, 65.1) * mm, "end": v(-25.18, 0) * mm, "construction": true});
            skLineSegment(sketch, "E118", {"start": v(-25.18, 3.11) * mm, "end": v(-35.18, 3.11) * mm, "construction": true});
            skCircle(sketch, "E119", {"center": v(-35.18, 3.11) * mm, "radius": 1.6 * mm});
            skCircle(sketch, "E120.MirrorC", {"center": v(-15.18, 3.11) * mm, "radius": 1.6 * mm});
            skSolve(sketch);
        }
        {
            var Q0;
            Q0 = qSketchRegion(id + "F23", true);
            extrude(context, id + "F24", {"entities" : qUnion([Q0]), "operationType" : NewBodyOperationType.REMOVE, "oppositeDirection" : true, "depth" : 25 * mm});
        }
        {
            var Q0;
            Q0=qCreatedBy(makeId("Right.planeOp"),FACE);
            var sketch = newSketch(context, id + "F25", { "sketchPlane" : qUnion([Q0])});
            skPoint(sketch, "E121.0", {"position": v(-75.54, 138) * mm});
            skCircle(sketch, "E122", {"center": v(-75.57, 143.33) * mm, "radius": 3.5 * mm});
            skSolve(sketch);
        }
        {
            var Q0;
            Q0 = qSketchRegion(id + "F25", true);
            extrude(context, id + "F26", {"entities" : qUnion([Q0]), "operationType" : NewBodyOperationType.ADD, "depth" : 5.2 * mm, "hasSecondDirection" : true, "secondDirectionOppositeDirection" : true, "secondDirectionDepth" : 55.2 * mm});
        }
    });
